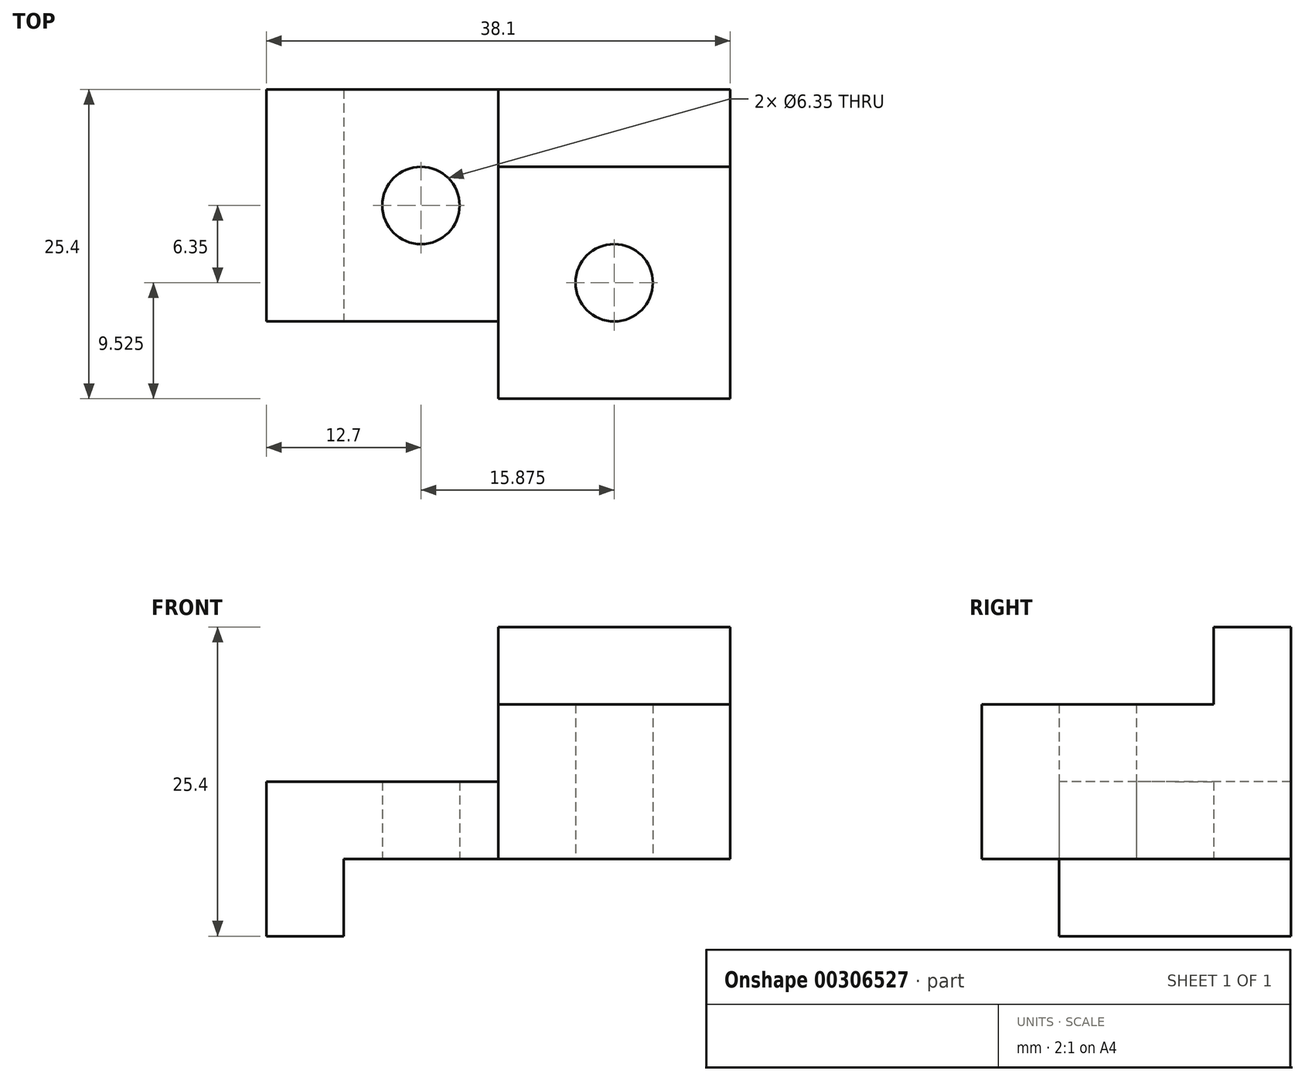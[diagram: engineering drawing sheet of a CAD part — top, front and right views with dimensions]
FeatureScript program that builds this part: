
annotation { "Feature Type Name" : "Feature", "Feature Type Description" : "" }
export const myFeature = defineFeature(function(context is Context, id is Id, definition is map)
    precondition{}
    {
        {
            var Q0;
            Q0=qCreatedBy(makeId("Top.planeOp"),FACE);
            var sketch = newSketch(context, id + "F0", { "sketchPlane" : qUnion([Q0])});
            skLineSegment(sketch, "E0.bottom", {"start": v(0, 0) * mm, "end": v(19.05, 0) * mm});
            skLineSegment(sketch, "E0.top", {"start": v(0, 19.05) * mm, "end": v(19.05, 19.05) * mm});
            skLineSegment(sketch, "E0.left", {"start": v(0, 0) * mm, "end": v(0, 19.05) * mm});
            skLineSegment(sketch, "E0.right", {"start": v(19.05, 0) * mm, "end": v(19.05, 19.05) * mm});
            skLineSegment(sketch, "E1.bottom", {"start": v(19.05, 19.05) * mm, "end": v(38.1, 19.05) * mm});
            skLineSegment(sketch, "E1.top", {"start": v(19.05, -6.35) * mm, "end": v(38.1, -6.35) * mm});
            skLineSegment(sketch, "E1.left", {"start": v(19.05, 19.05) * mm, "end": v(19.05, -6.35) * mm});
            skLineSegment(sketch, "E1.right", {"start": v(38.1, 19.05) * mm, "end": v(38.1, -6.35) * mm});
            skCircle(sketch, "E2", {"center": v(28.57, 3.18) * mm, "radius": 3.18 * mm});
            skCircle(sketch, "E3", {"center": v(12.7, 9.53) * mm, "radius": 3.18 * mm});
            skLineSegment(sketch, "E4", {"start": v(19.05, 12.7) * mm, "end": v(38.1, 12.7) * mm});
            skSolve(sketch);
        }
        {
            var Q0;
            Q0 = qSketchRegion(id + "F0", true);
            extrude(context, id + "F1", {"entities" : qUnion([Q0]), "depth" : 12.7 * mm});
        }
        {
            var Q0;
            {var subQ0=sQuery(id+"F0.wireOp",EDGE,"E1.bottom");Q0=makeQuery(id+"F0.imprint","IMPRINT",FACE,{"disambiguationData":[TD([[makeQuery(id+"F0.imprint","IMPRINT",EDGE,{"derivedFrom":subQ0}),-1.0]])]});}
            extrude(context, id + "F2", {"entities" : qUnion([Q0]), "operationType" : NewBodyOperationType.ADD, "depth" : 19.05 * mm});
        }
        {
            var Q0;
            Q0=makeQuery(id+"F1.opExtrude","SWEPT_FACE",FACE,{"disambiguationData":[OSD([sQuery(id+"F0.wireOp",EDGE,"E0.bottom")])]});
            var sketch = newSketch(context, id + "F3", { "sketchPlane" : qUnion([Q0])});
            skPoint(sketch, "E5", {"position": v(6.35, 0) * mm});
            skLineSegment(sketch, "E6.bottom", {"start": v(6.35, 0) * mm, "end": v(19.05, 0) * mm});
            skLineSegment(sketch, "E6.top", {"start": v(6.35, 6.35) * mm, "end": v(19.05, 6.35) * mm});
            skLineSegment(sketch, "E6.left", {"start": v(6.35, 0) * mm, "end": v(6.35, 6.35) * mm});
            skLineSegment(sketch, "E6.right", {"start": v(19.05, 0) * mm, "end": v(19.05, 6.35) * mm});
            skSolve(sketch);
        }
        {
            var Q0;
            Q0=makeQuery(id+"F3.imprint","IMPRINT",FACE,{"disambiguationData":[TD([[makeQuery(id+"F3.imprint","IMPRINT",EDGE,{"derivedFrom":sQuery(id+"F3.wireOp",EDGE,"E6.bottom")}),1.0]])]});
            extrude(context, id + "F4", {"entities" : qUnion([Q0]), "operationType" : NewBodyOperationType.REMOVE, "endBound" : BoundingType.THROUGH_ALL, "oppositeDirection" : true, "depth" : 25.4 * mm});
        }
        {
            var Q0;
            Q0=makeQuery(id+"F1.opExtrude","SWEPT_FACE",FACE,{"disambiguationData":[OSD([sQuery(id+"F0.wireOp",EDGE,"E1.top")])]});
            var sketch = newSketch(context, id + "F5", { "sketchPlane" : qUnion([Q0])});
            skLineSegment(sketch, "E7", {"start": v(19.05, 6.35) * mm, "end": v(38.1, 6.35) * mm});
            skSolve(sketch);
        }
        {
            var Q0;
            {var subQ0=sQuery(id+"F5.wireOp",EDGE,"E7");Q0=makeQuery(id+"F5.imprint","IMPRINT",FACE,{"disambiguationData":[TD([[makeQuery(id+"F5.imprint","IMPRINT",EDGE,{"derivedFrom":subQ0}),-1.0]])]});}
            extrude(context, id + "F6", {"entities" : qUnion([Q0]), "operationType" : NewBodyOperationType.REMOVE, "endBound" : BoundingType.THROUGH_ALL, "oppositeDirection" : true, "depth" : 25.4 * mm});
        }
        {
            var Q0;
            Q0=makeQuery(id+"F1.opExtrude","CAP_FACE",FACE,{"disambiguationData":[OSD([sQuery(id+"F0.wireOp",EDGE,"E0.bottom"),sQuery(id+"F0.wireOp",EDGE,"E0.top"),sQuery(id+"F0.wireOp",EDGE,"E0.left"),sQuery(id+"F0.wireOp",EDGE,"E1.bottom"),sQuery(id+"F0.wireOp",EDGE,"E1.top"),sQuery(id+"F0.wireOp",EDGE,"E1.left"),sQuery(id+"F0.wireOp",EDGE,"E1.right"),sQuery(id+"F0.wireOp",EDGE,"E2"),sQuery(id+"F0.wireOp",EDGE,"E3")])],"isStart":false});
            var sketch = newSketch(context, id + "F7", { "sketchPlane" : qUnion([Q0])});
            skLineSegment(sketch, "E8", {"start": v(19.05, 0) * mm, "end": v(19.05, 12.7) * mm});
            skSolve(sketch);
        }
        {
            var Q0;
            Q0=makeQuery(id+"F7.imprint","IMPRINT",FACE,{"disambiguationData":[TD([[makeQuery(id+"F7.imprint","IMPRINT",EDGE,{"derivedFrom":sQuery(id+"F7.wireOp",EDGE,"E8")}),-1.0]])]});
            extrude(context, id + "F8", {"entities" : qUnion([Q0]), "operationType" : NewBodyOperationType.ADD, "depth" : 6.35 * mm});
        }
        {
            var Q0;
            {var subQ0=sQuery(id+"F0.wireOp",EDGE,"E4");var subQ1=sQuery(id+"F0.wireOp",EDGE,"E1.right");var subQ2=sQuery(id+"F0.wireOp",EDGE,"E1.left");var subQ3=sQuery(id+"F0.wireOp",EDGE,"E1.bottom");Q0=makeQuery(id+"F8.boolean.opBoolean","MERGE",FACE,{"derivedFrom":[makeQuery(id+"F2.opExtrude","CAP_FACE",FACE,{"disambiguationData":[OSD([subQ3,subQ2,subQ1,subQ0])],"isStart":false}),makeQuery(id+"F8.opExtrude","CAP_FACE",FACE,{"disambiguationData":[OSD([sQuery(id+"F0.wireOp",EDGE,"E0.bottom"),sQuery(id+"F0.wireOp",EDGE,"E0.top"),sQuery(id+"F0.wireOp",EDGE,"E0.left"),subQ3,sQuery(id+"F0.wireOp",EDGE,"E1.top"),subQ2,subQ1,sQuery(id+"F0.wireOp",EDGE,"E2"),sQuery(id+"F0.wireOp",EDGE,"E3"),subQ0,sQuery(id+"F7.wireOp",EDGE,"E8")])],"isStart":false})]});}
            var sketch = newSketch(context, id + "F9", { "sketchPlane" : qUnion([Q0])});
            skLineSegment(sketch, "E9.bottom", {"start": v(19.05, 19.05) * mm, "end": v(38.1, 19.05) * mm});
            skLineSegment(sketch, "E9.top", {"start": v(19.05, 12.7) * mm, "end": v(38.1, 12.7) * mm});
            skLineSegment(sketch, "E9.left", {"start": v(19.05, 19.05) * mm, "end": v(19.05, 12.7) * mm});
            skLineSegment(sketch, "E9.right", {"start": v(38.1, 19.05) * mm, "end": v(38.1, 12.7) * mm});
            skSolve(sketch);
        }
        {
            var Q0;
            Q0 = qSketchRegion(id + "F9", true);
            extrude(context, id + "F10", {"entities" : qUnion([Q0]), "operationType" : NewBodyOperationType.ADD, "depth" : 6.35 * mm});
        }
    });
